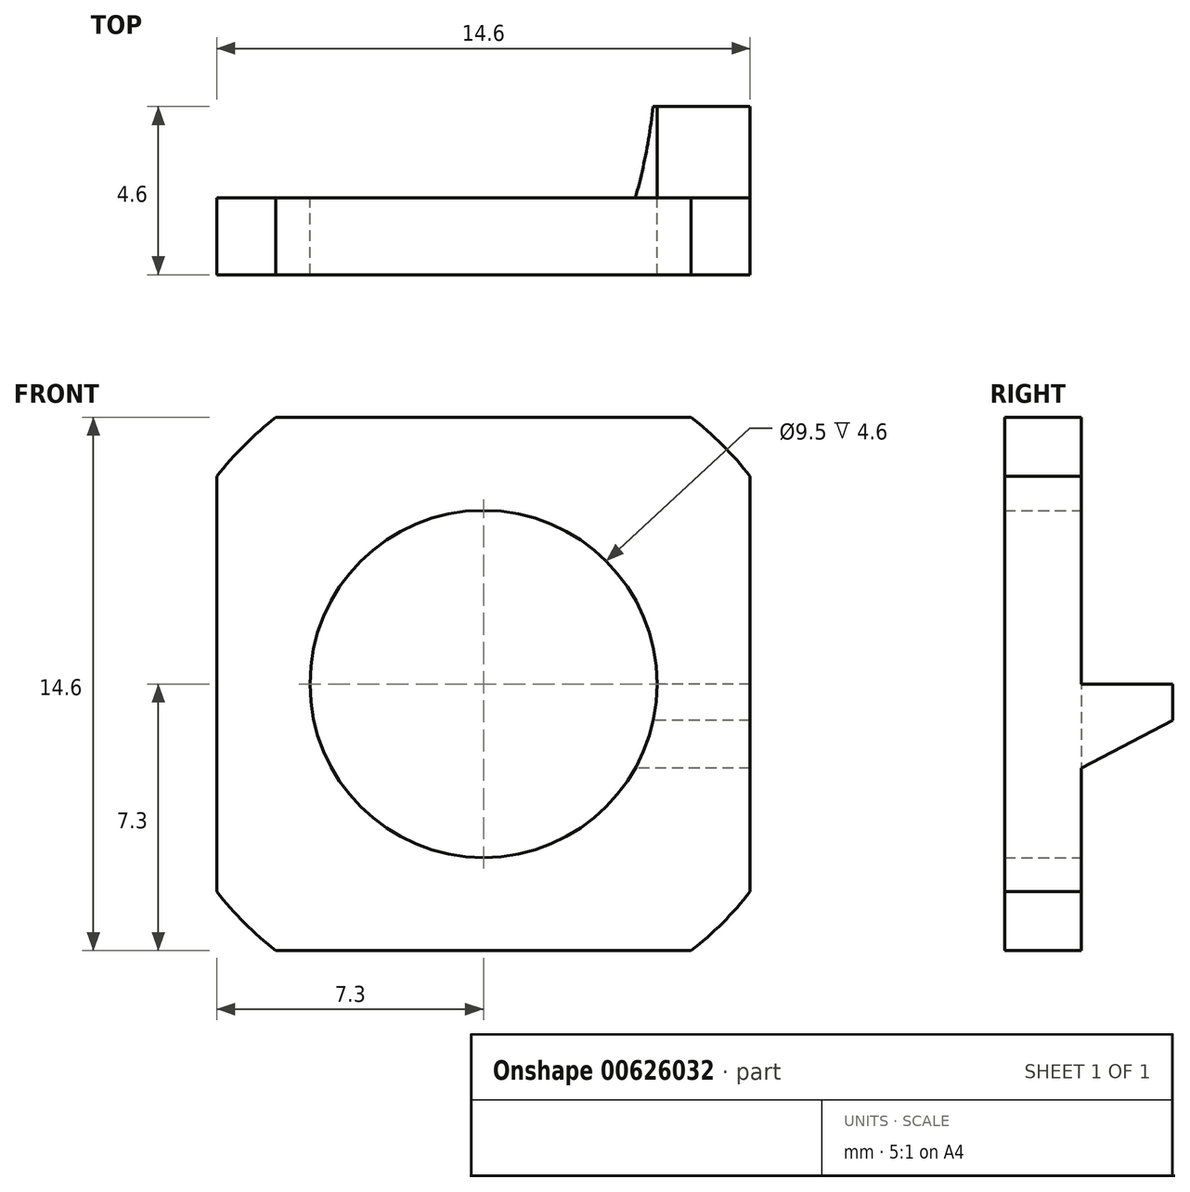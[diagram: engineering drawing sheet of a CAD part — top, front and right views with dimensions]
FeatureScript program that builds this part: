
annotation { "Feature Type Name" : "Feature", "Feature Type Description" : "" }
export const myFeature = defineFeature(function(context is Context, id is Id, definition is map)
    precondition{}
    {
        {
            var Q0;
            Q0=qCreatedBy(makeId("Front.planeOp"),FACE);
            var sketch = newSketch(context, id + "F0", { "sketchPlane" : qUnion([Q0])});
            skCircle(sketch, "E0", {"center": v(0, 0) * mm, "radius": 9.25 * mm});
            skCircle(sketch, "E1", {"center": v(0, 0) * mm, "radius": 4.75 * mm});
            skLineSegment(sketch, "E2", {"start": v(-7.3, 0) * mm, "end": v(-7.3, 7.3) * mm});
            skLineSegment(sketch, "E3", {"start": v(-7.3, 7.3) * mm, "end": v(7.3, 7.3) * mm});
            skLineSegment(sketch, "E4", {"start": v(7.3, 7.3) * mm, "end": v(7.3, 0) * mm});
            skLineSegment(sketch, "E5", {"start": v(7.3, 0) * mm, "end": v(7.3, -7.3) * mm});
            skLineSegment(sketch, "E6", {"start": v(7.3, -7.3) * mm, "end": v(-7.3, -7.3) * mm});
            skLineSegment(sketch, "E7", {"start": v(-7.3, -7.3) * mm, "end": v(-7.3, 0) * mm});
            skSolve(sketch);
        }
        {
            var Q0;
            {var subQ0=sQuery(id+"F0.wireOp",EDGE,"E3");var subQ1=sQuery(id+"F0.wireOp",EDGE,"E0");var subQ2=makeQuery(id+"F0.imprint","INTERSECT",VERTEX,{"disambiguationData":[OD(0.0)],"derivedFrom":[subQ1,subQ0]});Q0=makeQuery(id+"F0.imprint","IMPRINT",FACE,{"disambiguationData":[TD([[makeQuery(id+"F0.imprint","IMPRINT",EDGE,{"disambiguationData":[TD([[subQ2,-1.0]])],"derivedFrom":subQ1}),1.0]])]});}
            var Q1;
            {var subQ0=sQuery(id+"F0.wireOp",EDGE,"E2");var subQ1=sQuery(id+"F0.wireOp",EDGE,"E0");var subQ2=makeQuery(id+"F0.imprint","INTERSECT",VERTEX,{"derivedFrom":[subQ1,subQ0]});Q1=makeQuery(id+"F0.imprint","IMPRINT",FACE,{"disambiguationData":[TD([[makeQuery(id+"F0.imprint","IMPRINT",EDGE,{"disambiguationData":[TD([[subQ2,-1.0]])],"derivedFrom":subQ1}),1.0]])]});}
            var Q2;
            {var subQ0=sQuery(id+"F0.wireOp",EDGE,"E6");var subQ1=sQuery(id+"F0.wireOp",EDGE,"E0");var subQ2=makeQuery(id+"F0.imprint","INTERSECT",VERTEX,{"disambiguationData":[OD(0.0)],"derivedFrom":[subQ1,subQ0]});Q2=makeQuery(id+"F0.imprint","IMPRINT",FACE,{"disambiguationData":[TD([[makeQuery(id+"F0.imprint","IMPRINT",EDGE,{"disambiguationData":[TD([[subQ2,-1.0]])],"derivedFrom":subQ1}),1.0]])]});}
            var Q3;
            {var subQ0=sQuery(id+"F0.wireOp",EDGE,"E4");var subQ1=sQuery(id+"F0.wireOp",EDGE,"E0");var subQ2=makeQuery(id+"F0.imprint","INTERSECT",VERTEX,{"derivedFrom":[subQ1,subQ0]});Q3=makeQuery(id+"F0.imprint","IMPRINT",FACE,{"disambiguationData":[TD([[makeQuery(id+"F0.imprint","IMPRINT",EDGE,{"disambiguationData":[TD([[subQ2,1.0]])],"derivedFrom":subQ1}),1.0]])]});}
            var Q4;
            Q4=makeQuery(id+"F0.imprint","IMPRINT",FACE,{"disambiguationData":[TD([[makeQuery(id+"F0.imprint","IMPRINT",EDGE,{"derivedFrom":sQuery(id+"F0.wireOp",EDGE,"E1")}),-1.0]])]});
            extrude(context, id + "F1", {"entities" : qUnion([Q0, Q1, Q2, Q3, Q4]), "depth" : 2.1 * mm, "offsetDistance" : 25 * mm});
        }
        {
            var Q0;
            Q0=qCreatedBy(makeId("Right.planeOp"),FACE);
            var sketch = newSketch(context, id + "F2", { "sketchPlane" : qUnion([Q0])});
            skLineSegment(sketch, "E8", {"start": v(0, 0) * mm, "end": v(2.5, 0) * mm});
            skLineSegment(sketch, "E9", {"start": v(2.5, 0) * mm, "end": v(2.5, -1) * mm});
            skLineSegment(sketch, "E10", {"start": v(0, 0) * mm, "end": v(0, -2.3) * mm});
            skLineSegment(sketch, "E11", {"start": v(2.5, -1) * mm, "end": v(0, -2.3) * mm});
            skSolve(sketch);
        }
        {
            var Q0;
            Q0 = qSketchRegion(id + "F2", true);
            var Q1;
            Q1=makeQuery(id+"F1.opExtrude","SWEPT_FACE",FACE,{"disambiguationData":[OSD([sQuery(id+"F0.wireOp",EDGE,"E0")])]});
            extrude(context, id + "F3", {"entities" : qUnion([Q0]), "operationType" : NewBodyOperationType.ADD, "endBound" : BoundingType.UP_TO_SURFACE, "depth" : 9.97 * mm, "endBoundEntityFace" : qUnion([Q1]), "offsetDistance" : 25 * mm});
        }
        {
            var Q0;
            Q0=qCreatedBy(makeId("Front.planeOp"),FACE);
            var sketch = newSketch(context, id + "F4", { "sketchPlane" : qUnion([Q0])});
            skCircle(sketch, "E12.0", {"center": v(0, 0) * mm, "radius": 4.75 * mm});
            skSolve(sketch);
        }
        {
            var Q0;
            Q0=qCreatedBy(makeId("Front.planeOp"),FACE);
            var sketch = newSketch(context, id + "F5", { "sketchPlane" : qUnion([Q0])});
            skPoint(sketch, "E13.0", {"position": v(7.3, -7.3) * mm});
            skLineSegment(sketch, "E14.0", {"start": v(7.3, -7.3) * mm, "end": v(-7.3, -7.3) * mm});
            skLineSegment(sketch, "E15.0", {"start": v(7.3, 0) * mm, "end": v(7.3, -7.3) * mm});
            skLineSegment(sketch, "E16.0", {"start": v(7.3, 7.3) * mm, "end": v(7.3, 0) * mm});
            skLineSegment(sketch, "E17.0", {"start": v(-7.3, 7.3) * mm, "end": v(7.3, 7.3) * mm});
            skLineSegment(sketch, "E18.0", {"start": v(-7.3, 0) * mm, "end": v(-7.3, 7.3) * mm});
            skLineSegment(sketch, "E19.0", {"start": v(-7.3, -7.3) * mm, "end": v(-7.3, 0) * mm});
            skLineSegment(sketch, "E20.bottom", {"start": v(-10.4, 12.56) * mm, "end": v(9.88, 12.56) * mm});
            skLineSegment(sketch, "E20.top", {"start": v(-10.4, -12.56) * mm, "end": v(9.88, -12.56) * mm});
            skLineSegment(sketch, "E20.left", {"start": v(-10.4, 12.56) * mm, "end": v(-10.4, -12.56) * mm});
            skLineSegment(sketch, "E20.right", {"start": v(9.88, 12.56) * mm, "end": v(9.88, -12.56) * mm});
            skPoint(sketch, "E20.middle", {"position": v(-0.26, 0) * mm});
            skSolve(sketch);
        }
        {
            var Q0;
            Q0 = qSketchRegion(id + "F5", true);
            extrude(context, id + "F6", {"entities" : qUnion([Q0]), "operationType" : NewBodyOperationType.REMOVE, "depth" : 13.6 * mm, "offsetDistance" : 25 * mm});
        }
        {
            var Q0;
            Q0 = qSketchRegion(id + "F4", true);
            extrude(context, id + "F7", {"entities" : qUnion([Q0]), "operationType" : NewBodyOperationType.REMOVE, "oppositeDirection" : true, "depth" : 25 * mm, "offsetDistance" : 25 * mm});
        }
        {
            var Q0;
            {var subQ0=sQuery(id+"F0.wireOp",EDGE,"E3");var subQ1=sQuery(id+"F0.wireOp",EDGE,"E0");var subQ2=makeQuery(id+"F0.imprint","INTERSECT",VERTEX,{"disambiguationData":[OD(0.0)],"derivedFrom":[subQ1,subQ0]});Q0=makeQuery(id+"F0.imprint","IMPRINT",FACE,{"disambiguationData":[TD([[makeQuery(id+"F0.imprint","IMPRINT",EDGE,{"disambiguationData":[TD([[subQ2,-1.0]])],"derivedFrom":subQ1}),1.0]])]});}
            var Q1;
            {var subQ0=sQuery(id+"F0.wireOp",EDGE,"E4");var subQ1=sQuery(id+"F0.wireOp",EDGE,"E0");var subQ2=makeQuery(id+"F0.imprint","INTERSECT",VERTEX,{"derivedFrom":[subQ1,subQ0]});Q1=makeQuery(id+"F0.imprint","IMPRINT",FACE,{"disambiguationData":[TD([[makeQuery(id+"F0.imprint","IMPRINT",EDGE,{"disambiguationData":[TD([[subQ2,1.0]])],"derivedFrom":subQ1}),1.0]])]});}
            var Q2;
            {var subQ0=sQuery(id+"F0.wireOp",EDGE,"E6");var subQ1=sQuery(id+"F0.wireOp",EDGE,"E0");var subQ2=makeQuery(id+"F0.imprint","INTERSECT",VERTEX,{"disambiguationData":[OD(0.0)],"derivedFrom":[subQ1,subQ0]});Q2=makeQuery(id+"F0.imprint","IMPRINT",FACE,{"disambiguationData":[TD([[makeQuery(id+"F0.imprint","IMPRINT",EDGE,{"disambiguationData":[TD([[subQ2,-1.0]])],"derivedFrom":subQ1}),1.0]])]});}
            var Q3;
            {var subQ0=sQuery(id+"F0.wireOp",EDGE,"E2");var subQ1=sQuery(id+"F0.wireOp",EDGE,"E0");var subQ2=makeQuery(id+"F0.imprint","INTERSECT",VERTEX,{"derivedFrom":[subQ1,subQ0]});Q3=makeQuery(id+"F0.imprint","IMPRINT",FACE,{"disambiguationData":[TD([[makeQuery(id+"F0.imprint","IMPRINT",EDGE,{"disambiguationData":[TD([[subQ2,-1.0]])],"derivedFrom":subQ1}),1.0]])]});}
            extrude(context, id + "F8", {"entities" : qUnion([Q0, Q1, Q2, Q3]), "operationType" : NewBodyOperationType.REMOVE, "oppositeDirection" : true, "depth" : 9 * mm, "offsetDistance" : 25 * mm});
        }
    });
